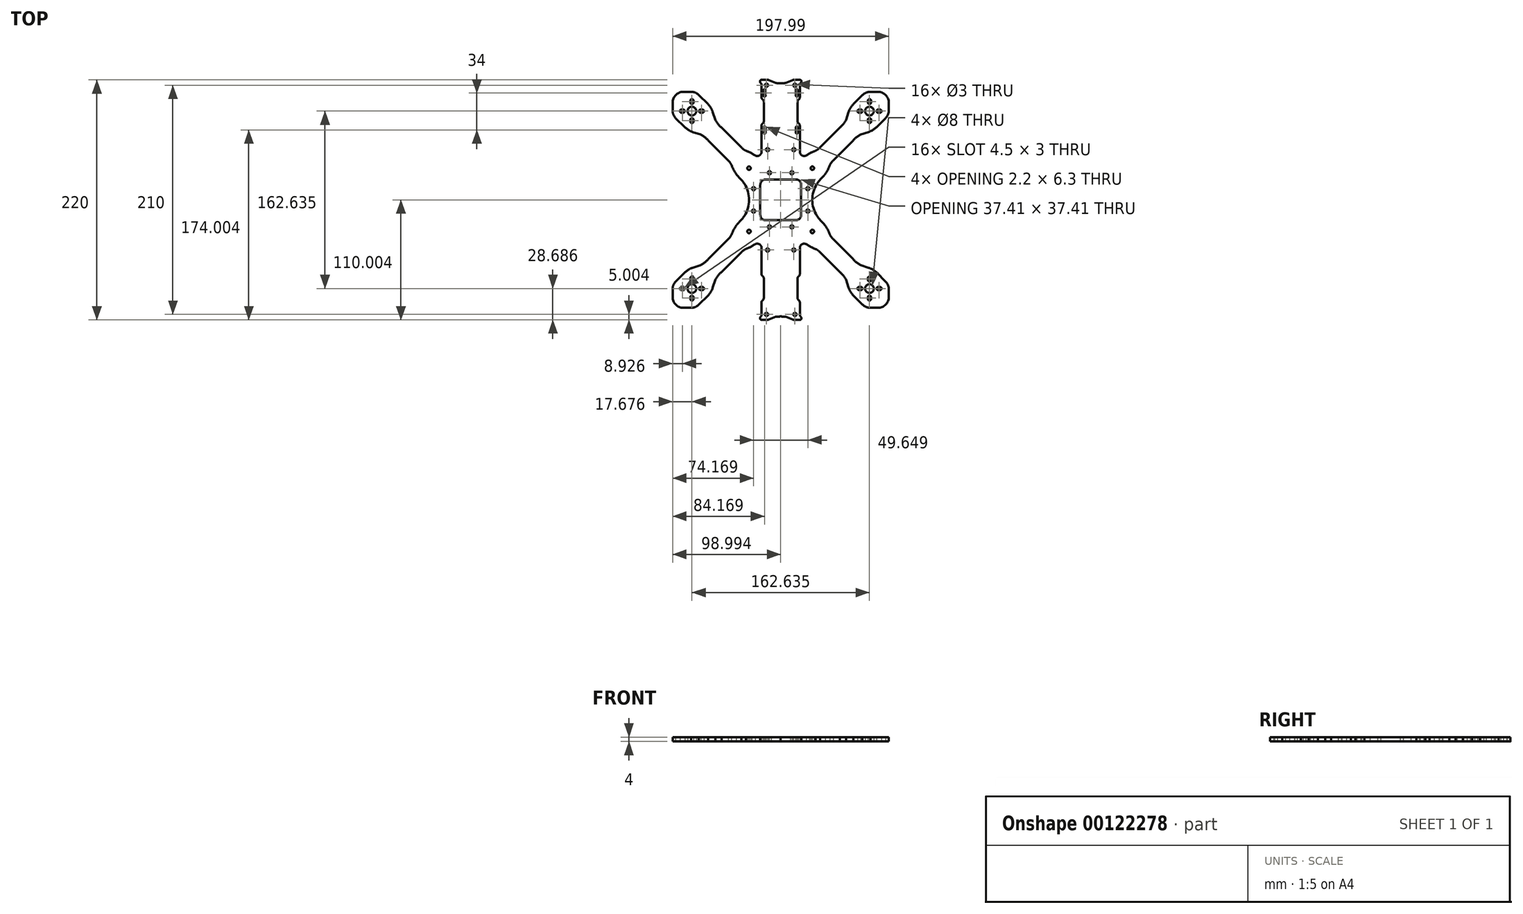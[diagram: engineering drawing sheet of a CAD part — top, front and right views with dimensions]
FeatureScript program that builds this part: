
annotation { "Feature Type Name" : "Feature", "Feature Type Description" : "" }
export const myFeature = defineFeature(function(context is Context, id is Id, definition is map)
    precondition{}
    {
        {
            var Q0;
            Q0=qCreatedBy(makeId("Top.planeOp"),FACE);
            var sketch = newSketch(context, id + "F0", { "sketchPlane" : qUnion([Q0])});
            skLineSegment(sketch, "E0", {"start": v(-69.83, -19.02) * mm, "end": v(-75.26, -19.02) * mm});
            skArc(sketch, "E1", {"start": v(-75.26, -19.02) * mm, "mid": v(-76.66, -19.98) * mm, "end": v(-76.26, -21.63) * mm});
            skLineSegment(sketch, "E2", {"start": v(-62.3, -21.8) * mm, "end": v(-68.72, -19.23) * mm});
            skArc(sketch, "E3", {"start": v(-75.26, -23.87) * mm, "mid": v(-75.52, -22.65) * mm, "end": v(-76.26, -21.63) * mm});
            skArc(sketch, "E4", {"start": v(-68.72, -19.23) * mm, "mid": v(-69.27, -19.07) * mm, "end": v(-69.83, -19.02) * mm});
            skArc(sketch, "E5", {"start": v(-62.3, -21.8) * mm, "mid": v(-61.75, -21.96) * mm, "end": v(-61.18, -22.02) * mm});
            skLineSegment(sketch, "E6", {"start": v(-61.18, -22.02) * mm, "end": v(-58.76, -22.02) * mm});
            skLineSegment(sketch, "E7", {"start": v(-73.26, -57.19) * mm, "end": v(-73.26, -38.84) * mm});
            skLineSegment(sketch, "E8", {"start": v(-73.84, -37.43) * mm, "end": v(-74.67, -36.6) * mm});
            skLineSegment(sketch, "E9", {"start": v(-74.67, -59.43) * mm, "end": v(-73.84, -58.6) * mm});
            skLineSegment(sketch, "E10", {"start": v(-75.26, -23.87) * mm, "end": v(-75.26, -35.19) * mm});
            skArc(sketch, "E11", {"start": v(-75.26, -35.19) * mm, "mid": v(-75.1, -35.95) * mm, "end": v(-74.67, -36.6) * mm});
            skArc(sketch, "E12", {"start": v(-73.26, -38.84) * mm, "mid": v(-73.4, -38.08) * mm, "end": v(-73.84, -37.43) * mm});
            skArc(sketch, "E13", {"start": v(-74.67, -59.43) * mm, "mid": v(-75.1, -60.08) * mm, "end": v(-75.26, -60.84) * mm});
            skArc(sketch, "E14", {"start": v(-73.84, -58.6) * mm, "mid": v(-73.4, -57.95) * mm, "end": v(-73.26, -57.19) * mm});
            skCircle(sketch, "E15", {"center": v(-139.07, -47.7) * mm, "radius": 4 * mm});
            skArc(sketch, "E16", {"start": v(-148.57, -46.2) * mm, "mid": v(-150.07, -47.7) * mm, "end": v(-148.57, -49.2) * mm});
            skArc(sketch, "E17", {"start": v(-147.07, -49.2) * mm, "mid": v(-145.57, -47.7) * mm, "end": v(-147.07, -46.2) * mm});
            skArc(sketch, "E18", {"start": v(-137.57, -38.2) * mm, "mid": v(-139.07, -36.7) * mm, "end": v(-140.57, -38.2) * mm});
            skArc(sketch, "E19", {"start": v(-140.57, -39.7) * mm, "mid": v(-139.07, -41.2) * mm, "end": v(-137.57, -39.7) * mm});
            skArc(sketch, "E20", {"start": v(-131.07, -46.2) * mm, "mid": v(-132.57, -47.7) * mm, "end": v(-131.07, -49.2) * mm});
            skArc(sketch, "E21", {"start": v(-129.57, -49.2) * mm, "mid": v(-128.07, -47.7) * mm, "end": v(-129.57, -46.2) * mm});
            skArc(sketch, "E22", {"start": v(-137.57, -55.7) * mm, "mid": v(-139.07, -54.2) * mm, "end": v(-140.57, -55.7) * mm});
            skArc(sketch, "E23", {"start": v(-140.57, -57.2) * mm, "mid": v(-139.07, -58.7) * mm, "end": v(-137.57, -57.2) * mm});
            skLineSegment(sketch, "E24", {"start": v(-148.57, -46.2) * mm, "end": v(-147.07, -46.2) * mm});
            skLineSegment(sketch, "E25", {"start": v(-147.07, -49.2) * mm, "end": v(-148.57, -49.2) * mm});
            skLineSegment(sketch, "E26", {"start": v(-140.57, -38.2) * mm, "end": v(-140.57, -39.7) * mm});
            skLineSegment(sketch, "E27", {"start": v(-137.57, -38.2) * mm, "end": v(-137.57, -39.7) * mm});
            skLineSegment(sketch, "E28", {"start": v(-129.57, -46.2) * mm, "end": v(-131.07, -46.2) * mm});
            skLineSegment(sketch, "E29", {"start": v(-129.57, -49.2) * mm, "end": v(-131.07, -49.2) * mm});
            skLineSegment(sketch, "E30", {"start": v(-137.57, -55.7) * mm, "end": v(-137.57, -57.2) * mm});
            skLineSegment(sketch, "E31", {"start": v(-140.57, -55.7) * mm, "end": v(-140.57, -57.2) * mm});
            skLineSegment(sketch, "E32", {"start": v(-124.22, -41.34) * mm, "end": v(-132.7, -32.85) * mm});
            skLineSegment(sketch, "E33", {"start": v(-153.92, -54.06) * mm, "end": v(-145.44, -62.55) * mm});
            skArc(sketch, "E34", {"start": v(-146.85, -30.02) * mm, "mid": v(-153.85, -32.92) * mm, "end": v(-156.75, -39.92) * mm});
            skLineSegment(sketch, "E35", {"start": v(-146.85, -30.02) * mm, "end": v(-139.78, -30.02) * mm});
            skLineSegment(sketch, "E36", {"start": v(-156.75, -39.92) * mm, "end": v(-156.75, -47) * mm});
            skLineSegment(sketch, "E37", {"start": v(-117.5, -55.83) * mm, "end": v(-119.98, -48.4) * mm});
            skLineSegment(sketch, "E38", {"start": v(-130.94, -69.27) * mm, "end": v(-138.37, -66.8) * mm});
            skArc(sketch, "E39", {"start": v(-123.87, -74.92) * mm, "mid": v(-127.1, -71.72) * mm, "end": v(-130.94, -69.27) * mm});
            skArc(sketch, "E40", {"start": v(-117.5, -55.83) * mm, "mid": v(-115.05, -59.66) * mm, "end": v(-111.85, -62.9) * mm});
            skArc(sketch, "E41", {"start": v(-119.98, -48.4) * mm, "mid": v(-121.73, -44.65) * mm, "end": v(-124.22, -41.34) * mm});
            skArc(sketch, "E42", {"start": v(-145.44, -62.55) * mm, "mid": v(-142.12, -65.04) * mm, "end": v(-138.37, -66.8) * mm});
            skArc(sketch, "E43", {"start": v(-132.7, -32.85) * mm, "mid": v(-135.96, -30.73) * mm, "end": v(-139.78, -30.02) * mm});
            skArc(sketch, "E44", {"start": v(-156.75, -47) * mm, "mid": v(-156.04, -50.8) * mm, "end": v(-153.92, -54.06) * mm});
            skCircle(sketch, "E45", {"center": v(-69.76, -83.02) * mm, "radius": 1.5 * mm});
            skLineSegment(sketch, "E46", {"start": v(-75.26, -60.84) * mm, "end": v(-75.26, -84.84) * mm});
            skArc(sketch, "E47", {"start": v(-102.83, -97.02) * mm, "mid": v(-104.16, -94.86) * mm, "end": v(-105.84, -92.95) * mm});
            skArc(sketch, "E48", {"start": v(-93.76, -81.02) * mm, "mid": v(-91.88, -82.65) * mm, "end": v(-89.75, -83.94) * mm});
            skCircle(sketch, "E49", {"center": v(-82.58, -118.73) * mm, "radius": 1.5 * mm});
            skCircle(sketch, "E50", {"center": v(-68.04, -104.2) * mm, "radius": 1.5 * mm});
            skLineSegment(sketch, "E51", {"start": v(-123.87, -74.92) * mm, "end": v(-105.84, -92.95) * mm});
            skLineSegment(sketch, "E52", {"start": v(-93.76, -81.02) * mm, "end": v(-111.85, -62.9) * mm});
            skCircle(sketch, "E53", {"center": v(-70.76, -24.02) * mm, "radius": 1.5 * mm});
            skCircle(sketch, "E54", {"center": v(-86.76, -100.02) * mm, "radius": 1.6 * mm});
            skArc(sketch, "E55", {"start": v(-98.64, -105.25) * mm, "mid": v(-97.14, -107.06) * mm, "end": v(-95.52, -108.78) * mm});
            skArc(sketch, "E56", {"start": v(-90.99, -114.37) * mm, "mid": v(-93.1, -111.46) * mm, "end": v(-95.52, -108.78) * mm});
            skArc(sketch, "E57", {"start": v(-81.52, -88.13) * mm, "mid": v(-85.5, -85.77) * mm, "end": v(-89.75, -83.94) * mm});
            skArc(sketch, "E58", {"start": v(-102.83, -97.02) * mm, "mid": v(-101, -101.27) * mm, "end": v(-98.64, -105.25) * mm});
            skArc(sketch, "E59", {"start": v(-81.52, -88.13) * mm, "mid": v(-77.4, -88.38) * mm, "end": v(-75.26, -84.84) * mm});
            skCircle(sketch, "E60", {"center": v(-139.07, -47.7) * mm, "radius": 14 * mm, "construction": true});
            skArc(sketch, "E61.MirrorCS", {"start": v(-40.26, -35.19) * mm, "mid": v(-40.4, -35.95) * mm, "end": v(-40.84, -36.6) * mm});
            skArc(sketch, "E62.MirrorCS", {"start": v(-40.84, -59.43) * mm, "mid": v(-40.4, -60.08) * mm, "end": v(-40.26, -60.84) * mm});
            skLineSegment(sketch, "E63.MirrorCS", {"start": v(-40.84, -59.43) * mm, "end": v(-41.67, -58.6) * mm});
            skArc(sketch, "E64.MirrorCS", {"start": v(33.06, -46.2) * mm, "mid": v(34.56, -47.7) * mm, "end": v(33.06, -49.2) * mm});
            skArc(sketch, "E65.MirrorCS", {"start": v(-41.67, -58.6) * mm, "mid": v(-42.1, -57.95) * mm, "end": v(-42.26, -57.19) * mm});
            skLineSegment(sketch, "E66.MirrorCS", {"start": v(22.06, -38.2) * mm, "end": v(22.06, -39.7) * mm});
            skLineSegment(sketch, "E67.MirrorCS", {"start": v(25.06, -38.2) * mm, "end": v(25.06, -39.7) * mm});
            skLineSegment(sketch, "E68.MirrorCS", {"start": v(31.56, -49.2) * mm, "end": v(33.06, -49.2) * mm});
            skLineSegment(sketch, "E69.MirrorCS", {"start": v(33.06, -46.2) * mm, "end": v(31.56, -46.2) * mm});
            skArc(sketch, "E70.MirrorCS", {"start": v(25.06, -39.7) * mm, "mid": v(23.56, -41.2) * mm, "end": v(22.06, -39.7) * mm});
            skArc(sketch, "E71.MirrorCS", {"start": v(22.06, -38.2) * mm, "mid": v(23.56, -36.7) * mm, "end": v(25.06, -38.2) * mm});
            skArc(sketch, "E72.MirrorCS", {"start": v(31.56, -49.2) * mm, "mid": v(30.06, -47.7) * mm, "end": v(31.56, -46.2) * mm});
            skLineSegment(sketch, "E73.MirrorCS", {"start": v(25.06, -55.7) * mm, "end": v(25.06, -57.2) * mm});
            skLineSegment(sketch, "E74.MirrorCS", {"start": v(-40.26, -23.87) * mm, "end": v(-40.26, -35.19) * mm});
            skLineSegment(sketch, "E75.MirrorCS", {"start": v(-41.67, -37.43) * mm, "end": v(-40.84, -36.6) * mm});
            skLineSegment(sketch, "E76.MirrorCS", {"start": v(-54.33, -22.02) * mm, "end": v(-56.76, -22.02) * mm});
            skArc(sketch, "E77.MirrorCS", {"start": v(-53.22, -21.8) * mm, "mid": v(-53.77, -21.96) * mm, "end": v(-54.33, -22.02) * mm});
            skArc(sketch, "E78.MirrorCS", {"start": v(-46.8, -19.23) * mm, "mid": v(-46.25, -19.07) * mm, "end": v(-45.68, -19.02) * mm});
            skArc(sketch, "E79.MirrorCS", {"start": v(-40.26, -23.87) * mm, "mid": v(-40, -22.65) * mm, "end": v(-39.26, -21.63) * mm});
            skLineSegment(sketch, "E80.MirrorCS", {"start": v(-53.22, -21.8) * mm, "end": v(-46.8, -19.23) * mm});
            skArc(sketch, "E81.MirrorCS", {"start": v(-40.26, -19.02) * mm, "mid": v(-38.86, -19.98) * mm, "end": v(-39.26, -21.63) * mm});
            skLineSegment(sketch, "E82.MirrorCS", {"start": v(-45.68, -19.02) * mm, "end": v(-40.26, -19.02) * mm});
            skArc(sketch, "E83.MirrorCS", {"start": v(-42.26, -38.84) * mm, "mid": v(-42.1, -38.08) * mm, "end": v(-41.67, -37.43) * mm});
            skLineSegment(sketch, "E84.MirrorCS", {"start": v(22.06, -55.7) * mm, "end": v(22.06, -57.2) * mm});
            skLineSegment(sketch, "E85.MirrorCS", {"start": v(14.06, -49.2) * mm, "end": v(15.56, -49.2) * mm});
            skCircle(sketch, "E86.MirrorC", {"center": v(-45.76, -83.02) * mm, "radius": 1.5 * mm});
            skArc(sketch, "E87.MirrorCS", {"start": v(-24.53, -114.37) * mm, "mid": v(-22.4, -111.46) * mm, "end": v(-20, -108.78) * mm});
            skArc(sketch, "E88.MirrorCS", {"start": v(17.2, -32.85) * mm, "mid": v(20.45, -30.73) * mm, "end": v(24.27, -30.02) * mm});
            skLineSegment(sketch, "E89.MirrorCS", {"start": v(14.06, -46.2) * mm, "end": v(15.56, -46.2) * mm});
            skArc(sketch, "E90.MirrorCS", {"start": v(41.24, -47) * mm, "mid": v(40.53, -50.8) * mm, "end": v(38.41, -54.06) * mm});
            skArc(sketch, "E91.MirrorCS", {"start": v(-16.87, -105.25) * mm, "mid": v(-18.38, -107.06) * mm, "end": v(-20, -108.78) * mm});
            skArc(sketch, "E92.MirrorCS", {"start": v(29.92, -62.55) * mm, "mid": v(26.61, -65.04) * mm, "end": v(22.85, -66.8) * mm});
            skArc(sketch, "E93.MirrorCS", {"start": v(4.47, -48.4) * mm, "mid": v(6.22, -44.65) * mm, "end": v(8.71, -41.34) * mm});
            skArc(sketch, "E94.MirrorCS", {"start": v(-21.76, -81.02) * mm, "mid": v(-23.63, -82.65) * mm, "end": v(-25.76, -83.94) * mm});
            skCircle(sketch, "E95.MirrorC", {"center": v(-44.76, -24.02) * mm, "radius": 1.5 * mm});
            skArc(sketch, "E96.MirrorCS", {"start": v(-12.68, -97.02) * mm, "mid": v(-11.35, -94.86) * mm, "end": v(-9.67, -92.95) * mm});
            skArc(sketch, "E97.MirrorCS", {"start": v(25.06, -57.2) * mm, "mid": v(23.56, -58.7) * mm, "end": v(22.06, -57.2) * mm});
            skArc(sketch, "E98.MirrorCS", {"start": v(22.06, -55.7) * mm, "mid": v(23.56, -54.2) * mm, "end": v(25.06, -55.7) * mm});
            skLineSegment(sketch, "E99.MirrorCS", {"start": v(15.43, -69.27) * mm, "end": v(22.85, -66.8) * mm});
            skLineSegment(sketch, "E100.MirrorCS", {"start": v(2, -55.83) * mm, "end": v(4.47, -48.4) * mm});
            skArc(sketch, "E101.MirrorCS", {"start": v(14.06, -49.2) * mm, "mid": v(12.56, -47.7) * mm, "end": v(14.06, -46.2) * mm});
            skArc(sketch, "E102.MirrorCS", {"start": v(15.56, -46.2) * mm, "mid": v(17.06, -47.7) * mm, "end": v(15.56, -49.2) * mm});
            skLineSegment(sketch, "E103.MirrorCS", {"start": v(31.34, -30.02) * mm, "end": v(24.27, -30.02) * mm});
            skCircle(sketch, "E104.MirrorC", {"center": v(23.56, -47.7) * mm, "radius": 4 * mm});
            skCircle(sketch, "E105.MirrorC", {"center": v(-47.47, -104.2) * mm, "radius": 1.5 * mm});
            skCircle(sketch, "E106.MirrorC", {"center": v(-32.93, -118.73) * mm, "radius": 1.5 * mm});
            skCircle(sketch, "E107.MirrorC", {"center": v(-28.76, -100.02) * mm, "radius": 1.6 * mm});
            skLineSegment(sketch, "E108.MirrorCS", {"start": v(8.36, -74.92) * mm, "end": v(-9.67, -92.95) * mm});
            skLineSegment(sketch, "E109.MirrorCS", {"start": v(38.41, -54.06) * mm, "end": v(29.92, -62.55) * mm});
            skLineSegment(sketch, "E110.MirrorCS", {"start": v(8.71, -41.34) * mm, "end": v(17.2, -32.85) * mm});
            skArc(sketch, "E111.MirrorCS", {"start": v(-34, -88.13) * mm, "mid": v(-38.12, -88.38) * mm, "end": v(-40.26, -84.84) * mm});
            skLineSegment(sketch, "E112.MirrorCS", {"start": v(-42.26, -57.19) * mm, "end": v(-42.26, -38.84) * mm});
            skArc(sketch, "E113.MirrorCS", {"start": v(-12.68, -97.02) * mm, "mid": v(-14.5, -101.27) * mm, "end": v(-16.87, -105.25) * mm});
            skArc(sketch, "E114.MirrorCS", {"start": v(-34, -88.13) * mm, "mid": v(-30.01, -85.77) * mm, "end": v(-25.76, -83.94) * mm});
            skCircle(sketch, "E115.MirrorC", {"center": v(23.56, -47.7) * mm, "radius": 14 * mm, "construction": true});
            skArc(sketch, "E116.MirrorCS", {"start": v(2, -55.83) * mm, "mid": v(-0.46, -59.66) * mm, "end": v(-3.66, -62.9) * mm});
            skArc(sketch, "E117.MirrorCS", {"start": v(8.36, -74.92) * mm, "mid": v(11.6, -71.72) * mm, "end": v(15.43, -69.27) * mm});
            skLineSegment(sketch, "E118.MirrorCS", {"start": v(-40.26, -60.84) * mm, "end": v(-40.26, -84.84) * mm});
            skLineSegment(sketch, "E119.MirrorCS", {"start": v(41.24, -39.92) * mm, "end": v(41.24, -47) * mm});
            skLineSegment(sketch, "E120.MirrorCS", {"start": v(-21.76, -81.02) * mm, "end": v(-3.66, -62.9) * mm});
            skArc(sketch, "E121.MirrorCS", {"start": v(31.34, -30.02) * mm, "mid": v(38.34, -32.92) * mm, "end": v(41.24, -39.92) * mm});
            skArc(sketch, "E122.MirrorCS", {"start": v(-57.76, -235.02) * mm, "mid": v(-57.46, -235.72) * mm, "end": v(-56.76, -236.02) * mm});
            skLineSegment(sketch, "E123.MirrorCS", {"start": v(-54.33, -236.02) * mm, "end": v(-56.76, -236.02) * mm});
            skArc(sketch, "E124.MirrorCS", {"start": v(-40.26, -222.84) * mm, "mid": v(-40.4, -222.08) * mm, "end": v(-40.84, -221.43) * mm});
            skLineSegment(sketch, "E125.MirrorCS", {"start": v(-61.18, -236.02) * mm, "end": v(-58.76, -236.02) * mm});
            skArc(sketch, "E126.MirrorCS", {"start": v(-57.76, -235.02) * mm, "mid": v(-58.05, -235.72) * mm, "end": v(-58.76, -236.02) * mm});
            skArc(sketch, "E127.MirrorCS", {"start": v(-75.26, -222.84) * mm, "mid": v(-75.1, -222.08) * mm, "end": v(-74.67, -221.43) * mm});
            skLineSegment(sketch, "E128.MirrorCS", {"start": v(-41.67, -220.6) * mm, "end": v(-40.84, -221.43) * mm});
            skArc(sketch, "E129.MirrorCS", {"start": v(-40.84, -198.6) * mm, "mid": v(-40.4, -197.95) * mm, "end": v(-40.26, -197.19) * mm});
            skLineSegment(sketch, "E130.MirrorCS", {"start": v(-74.67, -198.6) * mm, "end": v(-73.84, -199.43) * mm});
            skLineSegment(sketch, "E131.MirrorCS", {"start": v(-40.84, -198.6) * mm, "end": v(-41.67, -199.43) * mm});
            skArc(sketch, "E132.MirrorCS", {"start": v(-53.22, -236.23) * mm, "mid": v(-53.77, -236.07) * mm, "end": v(-54.33, -236.02) * mm});
            skLineSegment(sketch, "E133.MirrorCS", {"start": v(-137.57, -202.33) * mm, "end": v(-137.57, -200.83) * mm});
            skArc(sketch, "E134.MirrorCS", {"start": v(-41.67, -199.43) * mm, "mid": v(-42.1, -200.08) * mm, "end": v(-42.26, -200.84) * mm});
            skLineSegment(sketch, "E135.MirrorCS", {"start": v(-140.57, -202.33) * mm, "end": v(-140.57, -200.83) * mm});
            skArc(sketch, "E136.MirrorCS", {"start": v(-62.3, -236.23) * mm, "mid": v(-61.75, -236.07) * mm, "end": v(-61.18, -236.02) * mm});
            skArc(sketch, "E137.MirrorCS", {"start": v(-137.57, -202.33) * mm, "mid": v(-139.07, -203.83) * mm, "end": v(-140.57, -202.33) * mm});
            skArc(sketch, "E138.MirrorCS", {"start": v(-42.26, -219.19) * mm, "mid": v(-42.1, -219.95) * mm, "end": v(-41.67, -220.6) * mm});
            skLineSegment(sketch, "E139.MirrorCS", {"start": v(-73.84, -220.6) * mm, "end": v(-74.67, -221.43) * mm});
            skArc(sketch, "E140.MirrorCS", {"start": v(-74.67, -198.6) * mm, "mid": v(-75.1, -197.95) * mm, "end": v(-75.26, -197.19) * mm});
            skArc(sketch, "E141.MirrorCS", {"start": v(-46.8, -238.8) * mm, "mid": v(-46.25, -238.96) * mm, "end": v(-45.68, -239.02) * mm});
            skArc(sketch, "E142.MirrorCS", {"start": v(-140.57, -200.83) * mm, "mid": v(-139.07, -199.33) * mm, "end": v(-137.57, -200.83) * mm});
            skArc(sketch, "E143.MirrorCS", {"start": v(22.06, -202.33) * mm, "mid": v(23.56, -203.83) * mm, "end": v(25.06, -202.33) * mm});
            skArc(sketch, "E144.MirrorCS", {"start": v(-137.57, -219.83) * mm, "mid": v(-139.07, -221.33) * mm, "end": v(-140.57, -219.83) * mm});
            skLineSegment(sketch, "E145.MirrorCS", {"start": v(-129.57, -211.83) * mm, "end": v(-131.07, -211.83) * mm});
            skArc(sketch, "E146.MirrorCS", {"start": v(-140.57, -218.33) * mm, "mid": v(-139.07, -216.83) * mm, "end": v(-137.57, -218.33) * mm});
            skLineSegment(sketch, "E147.MirrorCS", {"start": v(14.06, -208.83) * mm, "end": v(15.56, -208.83) * mm});
            skLineSegment(sketch, "E148.MirrorCS", {"start": v(-129.57, -208.83) * mm, "end": v(-131.07, -208.83) * mm});
            skArc(sketch, "E149.MirrorCS", {"start": v(-131.07, -211.83) * mm, "mid": v(-132.57, -210.33) * mm, "end": v(-131.07, -208.83) * mm});
            skArc(sketch, "E150.MirrorCS", {"start": v(31.56, -208.83) * mm, "mid": v(30.06, -210.33) * mm, "end": v(31.56, -211.83) * mm});
            skArc(sketch, "E151.MirrorCS", {"start": v(33.06, -211.83) * mm, "mid": v(34.56, -210.33) * mm, "end": v(33.06, -208.83) * mm});
            skArc(sketch, "E152.MirrorCS", {"start": v(25.06, -200.83) * mm, "mid": v(23.56, -199.33) * mm, "end": v(22.06, -200.83) * mm});
            skLineSegment(sketch, "E153.MirrorCS", {"start": v(25.06, -202.33) * mm, "end": v(25.06, -200.83) * mm});
            skLineSegment(sketch, "E154.MirrorCS", {"start": v(-40.26, -234.16) * mm, "end": v(-40.26, -222.84) * mm});
            skLineSegment(sketch, "E155.MirrorCS", {"start": v(14.06, -211.83) * mm, "end": v(15.56, -211.83) * mm});
            skArc(sketch, "E156.MirrorCS", {"start": v(-148.57, -211.83) * mm, "mid": v(-150.07, -210.33) * mm, "end": v(-148.57, -208.83) * mm});
            skArc(sketch, "E157.MirrorCS", {"start": v(-147.07, -208.83) * mm, "mid": v(-145.57, -210.33) * mm, "end": v(-147.07, -211.83) * mm});
            skArc(sketch, "E158.MirrorCS", {"start": v(-40.26, -234.16) * mm, "mid": v(-40, -235.39) * mm, "end": v(-39.26, -236.4) * mm});
            skCircle(sketch, "E159.MirrorC", {"center": v(-44.76, -234.02) * mm, "radius": 1.5 * mm});
            skArc(sketch, "E160.MirrorCS", {"start": v(-68.72, -238.8) * mm, "mid": v(-69.27, -238.96) * mm, "end": v(-69.83, -239.02) * mm});
            skLineSegment(sketch, "E161.MirrorCS", {"start": v(-140.57, -219.83) * mm, "end": v(-140.57, -218.33) * mm});
            skArc(sketch, "E162.MirrorCS", {"start": v(15.56, -211.83) * mm, "mid": v(17.06, -210.33) * mm, "end": v(15.56, -208.83) * mm});
            skLineSegment(sketch, "E163.MirrorCS", {"start": v(-137.57, -219.83) * mm, "end": v(-137.57, -218.33) * mm});
            skLineSegment(sketch, "E164.MirrorCS", {"start": v(22.06, -219.83) * mm, "end": v(22.06, -218.33) * mm});
            skArc(sketch, "E165.MirrorCS", {"start": v(14.06, -208.83) * mm, "mid": v(12.56, -210.33) * mm, "end": v(14.06, -211.83) * mm});
            skArc(sketch, "E166.MirrorCS", {"start": v(25.06, -218.33) * mm, "mid": v(23.56, -216.83) * mm, "end": v(22.06, -218.33) * mm});
            skArc(sketch, "E167.MirrorCS", {"start": v(-129.57, -208.83) * mm, "mid": v(-128.07, -210.33) * mm, "end": v(-129.57, -211.83) * mm});
            skArc(sketch, "E168.MirrorCS", {"start": v(-73.26, -219.19) * mm, "mid": v(-73.4, -219.95) * mm, "end": v(-73.84, -220.6) * mm});
            skLineSegment(sketch, "E169.MirrorCS", {"start": v(-148.57, -211.83) * mm, "end": v(-147.07, -211.83) * mm});
            skArc(sketch, "E170.MirrorCS", {"start": v(-75.26, -239.02) * mm, "mid": v(-76.66, -238.05) * mm, "end": v(-76.26, -236.4) * mm});
            skLineSegment(sketch, "E171.MirrorCS", {"start": v(33.06, -211.83) * mm, "end": v(31.56, -211.83) * mm});
            skLineSegment(sketch, "E172.MirrorCS", {"start": v(-75.26, -234.16) * mm, "end": v(-75.26, -222.84) * mm});
            skArc(sketch, "E173.MirrorCS", {"start": v(22.06, -219.83) * mm, "mid": v(23.56, -221.33) * mm, "end": v(25.06, -219.83) * mm});
            skLineSegment(sketch, "E174.MirrorCS", {"start": v(22.06, -202.33) * mm, "end": v(22.06, -200.83) * mm});
            skLineSegment(sketch, "E175.MirrorCS", {"start": v(-147.07, -208.83) * mm, "end": v(-148.57, -208.83) * mm});
            skLineSegment(sketch, "E176.MirrorCS", {"start": v(-69.83, -239.02) * mm, "end": v(-75.26, -239.02) * mm});
            skLineSegment(sketch, "E177.MirrorCS", {"start": v(31.56, -208.83) * mm, "end": v(33.06, -208.83) * mm});
            skArc(sketch, "E178.MirrorCS", {"start": v(-75.26, -234.16) * mm, "mid": v(-75.52, -235.39) * mm, "end": v(-76.26, -236.4) * mm});
            skLineSegment(sketch, "E179.MirrorCS", {"start": v(25.06, -219.83) * mm, "end": v(25.06, -218.33) * mm});
            skLineSegment(sketch, "E180.MirrorCS", {"start": v(-62.3, -236.23) * mm, "end": v(-68.72, -238.8) * mm});
            skLineSegment(sketch, "E181.MirrorCS", {"start": v(-53.22, -236.23) * mm, "end": v(-46.8, -238.8) * mm});
            skArc(sketch, "E182.MirrorCS", {"start": v(-73.84, -199.43) * mm, "mid": v(-73.4, -200.08) * mm, "end": v(-73.26, -200.84) * mm});
            skArc(sketch, "E183.MirrorCS", {"start": v(41.24, -211.04) * mm, "mid": v(40.53, -207.22) * mm, "end": v(38.41, -203.97) * mm});
            skLineSegment(sketch, "E184.MirrorCS", {"start": v(15.43, -188.77) * mm, "end": v(22.85, -191.24) * mm});
            skArc(sketch, "E185.MirrorCS", {"start": v(-16.87, -152.79) * mm, "mid": v(-18.38, -150.97) * mm, "end": v(-20, -149.25) * mm});
            skLineSegment(sketch, "E186.MirrorCS", {"start": v(41.24, -218.11) * mm, "end": v(41.24, -211.04) * mm});
            skArc(sketch, "E187.MirrorCS", {"start": v(-156.75, -211.04) * mm, "mid": v(-156.04, -207.22) * mm, "end": v(-153.92, -203.97) * mm});
            skLineSegment(sketch, "E188.MirrorCS", {"start": v(-146.85, -228.01) * mm, "end": v(-139.78, -228.01) * mm});
            skCircle(sketch, "E189.MirrorC", {"center": v(-69.76, -175.02) * mm, "radius": 1.5 * mm});
            skArc(sketch, "E190.MirrorCS", {"start": v(-81.52, -169.9) * mm, "mid": v(-85.5, -172.27) * mm, "end": v(-89.75, -174.1) * mm});
            skCircle(sketch, "E191.MirrorC", {"center": v(-45.76, -175.02) * mm, "radius": 1.5 * mm});
            skArc(sketch, "E192.MirrorCS", {"start": v(2, -202.2) * mm, "mid": v(-0.46, -198.37) * mm, "end": v(-3.66, -195.13) * mm});
            skLineSegment(sketch, "E193.MirrorCS", {"start": v(31.34, -228.01) * mm, "end": v(24.27, -228.01) * mm});
            skArc(sketch, "E194.MirrorCS", {"start": v(-102.83, -161.01) * mm, "mid": v(-101, -156.76) * mm, "end": v(-98.64, -152.79) * mm});
            skArc(sketch, "E195.MirrorCS", {"start": v(-24.53, -143.67) * mm, "mid": v(-22.4, -146.58) * mm, "end": v(-20, -149.25) * mm});
            skArc(sketch, "E196.MirrorCS", {"start": v(8.36, -183.11) * mm, "mid": v(11.6, -186.31) * mm, "end": v(15.43, -188.77) * mm});
            skCircle(sketch, "E197.MirrorC", {"center": v(23.56, -210.33) * mm, "radius": 4 * mm});
            skArc(sketch, "E198.MirrorCS", {"start": v(-81.52, -169.9) * mm, "mid": v(-77.4, -169.66) * mm, "end": v(-75.26, -173.2) * mm});
            skArc(sketch, "E199.MirrorCS", {"start": v(17.2, -225.18) * mm, "mid": v(20.45, -227.3) * mm, "end": v(24.27, -228.01) * mm});
            skCircle(sketch, "E200.MirrorC", {"center": v(-139.07, -210.33) * mm, "radius": 4 * mm});
            skArc(sketch, "E201.MirrorCS", {"start": v(29.92, -195.48) * mm, "mid": v(26.61, -193) * mm, "end": v(22.85, -191.24) * mm});
            skArc(sketch, "E202.MirrorCS", {"start": v(-90.99, -143.67) * mm, "mid": v(-93.1, -146.58) * mm, "end": v(-95.52, -149.25) * mm});
            skArc(sketch, "E203.MirrorCS", {"start": v(-21.76, -177.02) * mm, "mid": v(-23.63, -175.38) * mm, "end": v(-25.76, -174.1) * mm});
            skLineSegment(sketch, "E204.MirrorCS", {"start": v(-156.75, -218.11) * mm, "end": v(-156.75, -211.04) * mm});
            skArc(sketch, "E205.MirrorCS", {"start": v(-117.5, -202.2) * mm, "mid": v(-115.05, -198.37) * mm, "end": v(-111.85, -195.13) * mm});
            skLineSegment(sketch, "E206.MirrorCS", {"start": v(2, -202.2) * mm, "end": v(4.47, -209.63) * mm});
            skArc(sketch, "E207.MirrorCS", {"start": v(-119.98, -209.63) * mm, "mid": v(-121.73, -213.39) * mm, "end": v(-124.22, -216.7) * mm});
            skArc(sketch, "E208.MirrorCS", {"start": v(-132.7, -225.18) * mm, "mid": v(-135.96, -227.3) * mm, "end": v(-139.78, -228.01) * mm});
            skArc(sketch, "E209.MirrorCS", {"start": v(-34, -169.9) * mm, "mid": v(-30.01, -172.27) * mm, "end": v(-25.76, -174.1) * mm});
            skCircle(sketch, "E210.MirrorC", {"center": v(-70.76, -234.02) * mm, "radius": 1.5 * mm});
            skLineSegment(sketch, "E211.MirrorCS", {"start": v(-45.68, -239.02) * mm, "end": v(-40.26, -239.02) * mm});
            skArc(sketch, "E212.MirrorCS", {"start": v(-34, -169.9) * mm, "mid": v(-38.12, -169.66) * mm, "end": v(-40.26, -173.2) * mm});
            skLineSegment(sketch, "E213.MirrorCS", {"start": v(-130.94, -188.77) * mm, "end": v(-138.37, -191.24) * mm});
            skArc(sketch, "E214.MirrorCS", {"start": v(-93.76, -177.02) * mm, "mid": v(-91.88, -175.38) * mm, "end": v(-89.75, -174.1) * mm});
            skArc(sketch, "E215.MirrorCS", {"start": v(-102.83, -161.01) * mm, "mid": v(-104.16, -163.18) * mm, "end": v(-105.84, -165.08) * mm});
            skArc(sketch, "E216.MirrorCS", {"start": v(-145.44, -195.48) * mm, "mid": v(-142.12, -193) * mm, "end": v(-138.37, -191.24) * mm});
            skArc(sketch, "E217.MirrorCS", {"start": v(4.47, -209.63) * mm, "mid": v(6.22, -213.39) * mm, "end": v(8.71, -216.7) * mm});
            skLineSegment(sketch, "E218.MirrorCS", {"start": v(-117.5, -202.2) * mm, "end": v(-119.98, -209.63) * mm});
            skArc(sketch, "E219.MirrorCS", {"start": v(-98.64, -152.79) * mm, "mid": v(-97.14, -150.97) * mm, "end": v(-95.52, -149.25) * mm});
            skArc(sketch, "E220.MirrorCS", {"start": v(-123.87, -183.11) * mm, "mid": v(-127.1, -186.31) * mm, "end": v(-130.94, -188.77) * mm});
            skArc(sketch, "E221.MirrorCS", {"start": v(-12.68, -161.01) * mm, "mid": v(-14.5, -156.76) * mm, "end": v(-16.87, -152.79) * mm});
            skArc(sketch, "E222.MirrorCS", {"start": v(-12.68, -161.01) * mm, "mid": v(-11.35, -163.18) * mm, "end": v(-9.67, -165.08) * mm});
            skArc(sketch, "E223.MirrorCS", {"start": v(-40.26, -239.02) * mm, "mid": v(-38.86, -238.05) * mm, "end": v(-39.26, -236.4) * mm});
            skLineSegment(sketch, "E224.MirrorCS", {"start": v(38.41, -203.97) * mm, "end": v(29.92, -195.48) * mm});
            skCircle(sketch, "E225.MirrorC", {"center": v(-47.47, -153.84) * mm, "radius": 1.5 * mm});
            skCircle(sketch, "E226.MirrorC", {"center": v(-32.93, -139.3) * mm, "radius": 1.5 * mm});
            skCircle(sketch, "E227.MirrorC", {"center": v(-28.76, -158.02) * mm, "radius": 1.6 * mm});
            skCircle(sketch, "E228.MirrorC", {"center": v(-86.76, -158.02) * mm, "radius": 1.6 * mm});
            skCircle(sketch, "E229.MirrorC", {"center": v(-82.58, -139.3) * mm, "radius": 1.5 * mm});
            skCircle(sketch, "E230.MirrorC", {"center": v(-68.04, -153.84) * mm, "radius": 1.5 * mm});
            skLineSegment(sketch, "E231.MirrorCS", {"start": v(-123.87, -183.11) * mm, "end": v(-105.84, -165.08) * mm});
            skArc(sketch, "E232.MirrorCS", {"start": v(-146.85, -228.01) * mm, "mid": v(-153.85, -225.11) * mm, "end": v(-156.75, -218.11) * mm});
            skLineSegment(sketch, "E233.MirrorCS", {"start": v(-93.76, -177.02) * mm, "end": v(-111.85, -195.13) * mm});
            skLineSegment(sketch, "E234.MirrorCS", {"start": v(8.36, -183.11) * mm, "end": v(-9.67, -165.08) * mm});
            skLineSegment(sketch, "E235.MirrorCS", {"start": v(-40.26, -197.19) * mm, "end": v(-40.26, -173.2) * mm});
            skLineSegment(sketch, "E236.MirrorCS", {"start": v(-124.22, -216.7) * mm, "end": v(-132.7, -225.18) * mm});
            skLineSegment(sketch, "E237.MirrorCS", {"start": v(-153.92, -203.97) * mm, "end": v(-145.44, -195.48) * mm});
            skLineSegment(sketch, "E238.MirrorCS", {"start": v(-42.26, -200.84) * mm, "end": v(-42.26, -219.19) * mm});
            skLineSegment(sketch, "E239.MirrorCS", {"start": v(-75.26, -197.19) * mm, "end": v(-75.26, -173.2) * mm});
            skCircle(sketch, "E240.MirrorC", {"center": v(-139.07, -210.33) * mm, "radius": 14 * mm, "construction": true});
            skLineSegment(sketch, "E241.MirrorCS", {"start": v(8.71, -216.7) * mm, "end": v(17.2, -225.18) * mm});
            skLineSegment(sketch, "E242.MirrorCS", {"start": v(-21.76, -177.02) * mm, "end": v(-3.66, -195.13) * mm});
            skLineSegment(sketch, "E243.MirrorCS", {"start": v(-73.26, -200.84) * mm, "end": v(-73.26, -219.19) * mm});
            skArc(sketch, "E244.MirrorCS", {"start": v(31.34, -228.01) * mm, "mid": v(38.34, -225.11) * mm, "end": v(41.24, -218.11) * mm});
            skCircle(sketch, "E245.MirrorC", {"center": v(23.56, -210.33) * mm, "radius": 14 * mm, "construction": true});
            skLineSegment(sketch, "E246.bottom", {"start": v(-71.46, -110.3) * mm, "end": v(-44.05, -110.3) * mm});
            skLineSegment(sketch, "E246.top", {"start": v(-71.46, -147.72) * mm, "end": v(-44.05, -147.72) * mm});
            skLineSegment(sketch, "E246.left", {"start": v(-76.46, -115.3) * mm, "end": v(-76.46, -142.72) * mm});
            skLineSegment(sketch, "E246.right", {"start": v(-39.05, -115.3) * mm, "end": v(-39.05, -142.72) * mm});
            skArc(sketch, "E247", {"start": v(-90.99, -143.67) * mm, "mid": v(-86.67, -129.02) * mm, "end": v(-90.99, -114.37) * mm});
            skArc(sketch, "E248", {"start": v(-24.53, -114.37) * mm, "mid": v(-28.85, -129.02) * mm, "end": v(-24.53, -143.67) * mm});
            skLineSegment(sketch, "E249.bottom", {"start": v(-72.93, -27.87) * mm, "end": v(-72.23, -27.87) * mm});
            skLineSegment(sketch, "E249.top", {"start": v(-72.93, -34.17) * mm, "end": v(-72.23, -34.17) * mm});
            skLineSegment(sketch, "E249.left", {"start": v(-73.68, -28.62) * mm, "end": v(-73.68, -33.42) * mm});
            skLineSegment(sketch, "E249.right", {"start": v(-71.48, -28.62) * mm, "end": v(-71.48, -33.42) * mm});
            skArc(sketch, "E250.filletArc", {"start": v(-72.93, -27.87) * mm, "mid": v(-73.46, -28.09) * mm, "end": v(-73.68, -28.62) * mm});
            skArc(sketch, "E251.filletArc", {"start": v(-71.48, -28.62) * mm, "mid": v(-71.7, -28.09) * mm, "end": v(-72.23, -27.87) * mm});
            skArc(sketch, "E252.filletArc", {"start": v(-73.68, -33.42) * mm, "mid": v(-73.46, -33.95) * mm, "end": v(-72.93, -34.17) * mm});
            skArc(sketch, "E253.filletArc", {"start": v(-72.23, -34.17) * mm, "mid": v(-71.7, -33.95) * mm, "end": v(-71.48, -33.42) * mm});
            skLineSegment(sketch, "E254.bottom", {"start": v(-72.93, -61.87) * mm, "end": v(-72.23, -61.87) * mm});
            skLineSegment(sketch, "E254.top", {"start": v(-72.93, -68.17) * mm, "end": v(-72.23, -68.17) * mm});
            skLineSegment(sketch, "E254.left", {"start": v(-73.68, -62.62) * mm, "end": v(-73.68, -67.42) * mm});
            skLineSegment(sketch, "E254.right", {"start": v(-71.48, -62.62) * mm, "end": v(-71.48, -67.42) * mm});
            skArc(sketch, "E255.filletArc", {"start": v(-72.93, -61.87) * mm, "mid": v(-73.46, -62.09) * mm, "end": v(-73.68, -62.62) * mm});
            skArc(sketch, "E256.filletArc", {"start": v(-71.48, -62.62) * mm, "mid": v(-71.7, -62.09) * mm, "end": v(-72.23, -61.87) * mm});
            skArc(sketch, "E257.filletArc", {"start": v(-73.68, -67.42) * mm, "mid": v(-73.46, -67.95) * mm, "end": v(-72.93, -68.17) * mm});
            skArc(sketch, "E258.filletArc", {"start": v(-72.23, -68.17) * mm, "mid": v(-71.7, -67.95) * mm, "end": v(-71.48, -67.42) * mm});
            skLineSegment(sketch, "E259.MirrorCS", {"start": v(-42.58, -68.17) * mm, "end": v(-43.28, -68.17) * mm});
            skLineSegment(sketch, "E260.MirrorCS", {"start": v(-42.58, -61.87) * mm, "end": v(-43.28, -61.87) * mm});
            skArc(sketch, "E261.MirrorCS", {"start": v(-42.58, -61.87) * mm, "mid": v(-42.05, -62.09) * mm, "end": v(-41.83, -62.62) * mm});
            skLineSegment(sketch, "E262.MirrorCS", {"start": v(-44.03, -62.62) * mm, "end": v(-44.03, -67.42) * mm});
            skArc(sketch, "E263.MirrorCS", {"start": v(-43.28, -68.17) * mm, "mid": v(-43.81, -67.95) * mm, "end": v(-44.03, -67.42) * mm});
            skArc(sketch, "E264.MirrorCS", {"start": v(-44.03, -62.62) * mm, "mid": v(-43.81, -62.09) * mm, "end": v(-43.28, -61.87) * mm});
            skArc(sketch, "E265.MirrorCS", {"start": v(-41.83, -67.42) * mm, "mid": v(-42.05, -67.95) * mm, "end": v(-42.58, -68.17) * mm});
            skLineSegment(sketch, "E266.MirrorCS", {"start": v(-41.83, -62.62) * mm, "end": v(-41.83, -67.42) * mm});
            skLineSegment(sketch, "E267.MirrorCS", {"start": v(-42.58, -34.17) * mm, "end": v(-43.28, -34.17) * mm});
            skLineSegment(sketch, "E268.MirrorCS", {"start": v(-42.58, -27.87) * mm, "end": v(-43.28, -27.87) * mm});
            skLineSegment(sketch, "E269.MirrorCS", {"start": v(-41.83, -28.62) * mm, "end": v(-41.83, -33.42) * mm});
            skLineSegment(sketch, "E270.MirrorCS", {"start": v(-44.03, -28.62) * mm, "end": v(-44.03, -33.42) * mm});
            skArc(sketch, "E271.MirrorCS", {"start": v(-44.03, -28.62) * mm, "mid": v(-43.81, -28.09) * mm, "end": v(-43.28, -27.87) * mm});
            skArc(sketch, "E272.MirrorCS", {"start": v(-41.83, -33.42) * mm, "mid": v(-42.05, -33.95) * mm, "end": v(-42.58, -34.17) * mm});
            skArc(sketch, "E273.MirrorCS", {"start": v(-43.28, -34.17) * mm, "mid": v(-43.81, -33.95) * mm, "end": v(-44.03, -33.42) * mm});
            skArc(sketch, "E274.MirrorCS", {"start": v(-42.58, -27.87) * mm, "mid": v(-42.05, -28.09) * mm, "end": v(-41.83, -28.62) * mm});
            skLineSegment(sketch, "E275", {"start": v(-56.76, -22.02) * mm, "end": v(-58.76, -22.02) * mm});
            skPoint(sketch, "E276.visualSharp", {"position": v(-76.46, -110.3) * mm});
            skArc(sketch, "E276.filletArc", {"start": v(-71.46, -110.3) * mm, "mid": v(-75, -111.77) * mm, "end": v(-76.46, -115.3) * mm});
            skPoint(sketch, "E277.visualSharp", {"position": v(-39.05, -110.3) * mm});
            skArc(sketch, "E277.filletArc", {"start": v(-39.05, -115.3) * mm, "mid": v(-40.51, -111.77) * mm, "end": v(-44.05, -110.3) * mm});
            skPoint(sketch, "E278.visualSharp", {"position": v(-39.05, -147.72) * mm});
            skArc(sketch, "E278.filletArc", {"start": v(-44.05, -147.72) * mm, "mid": v(-40.51, -146.26) * mm, "end": v(-39.05, -142.72) * mm});
            skPoint(sketch, "E279.visualSharp", {"position": v(-76.46, -147.72) * mm});
            skArc(sketch, "E279.filletArc", {"start": v(-76.46, -142.72) * mm, "mid": v(-75, -146.26) * mm, "end": v(-71.46, -147.72) * mm});
            skSolve(sketch);
        }
        {
            var Q0;
            Q0=qSketchRegion(id+"F0",true);
            extrude(context, id + "F1", {"entities" : qUnion([Q0]), "depth" : 4 * mm});
        }
    });
